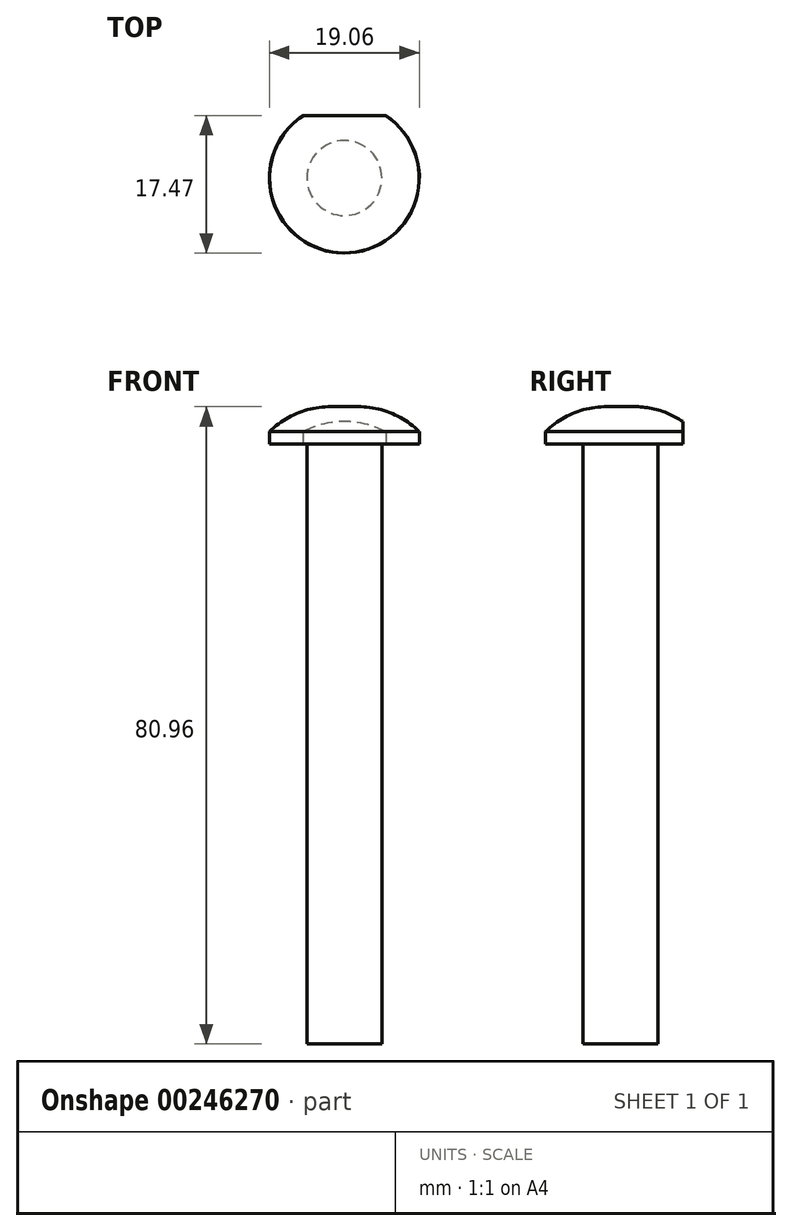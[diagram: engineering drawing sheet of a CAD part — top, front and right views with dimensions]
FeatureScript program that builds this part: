
annotation { "Feature Type Name" : "Feature", "Feature Type Description" : "" }
export const myFeature = defineFeature(function(context is Context, id is Id, definition is map)
    precondition{}
    {
        {
            var Q0;
            Q0=qCreatedBy(makeId("Front.planeOp"),FACE);
            var sketch = newSketch(context, id + "F0", { "sketchPlane" : qUnion([Q0])});
            skLineSegment(sketch, "E0", {"start": v(0, 0) * mm, "end": v(0, 76.2) * mm});
            skLineSegment(sketch, "E1", {"start": v(0, 76.2) * mm, "end": v(0, 77.79) * mm});
            skLineSegment(sketch, "E2", {"start": v(0, 77.79) * mm, "end": v(0, 80.96) * mm});
            skLineSegment(sketch, "E3", {"start": v(0, 80.96) * mm, "end": v(1.72, 80.96) * mm});
            skLineSegment(sketch, "E4", {"start": v(0, 77.79) * mm, "end": v(9.53, 77.79) * mm});
            skPoint(sketch, "E5.visualSharp", {"position": v(6.65, 80.96) * mm});
            skArc(sketch, "E5.filletArc", {"start": v(9.5, 77.79) * mm, "mid": v(5.92, 80.14) * mm, "end": v(1.72, 80.96) * mm});
            skLineSegment(sketch, "E6", {"start": v(0, 76.2) * mm, "end": v(9.53, 76.2) * mm});
            skLineSegment(sketch, "E7", {"start": v(9.53, 76.2) * mm, "end": v(9.53, 77.79) * mm});
            skLineSegment(sketch, "E8", {"start": v(0, 0) * mm, "end": v(4.76, 0) * mm});
            skLineSegment(sketch, "E9", {"start": v(4.76, 0) * mm, "end": v(4.76, 76.2) * mm});
            skSolve(sketch);
        }
        {
            var Q0;
            {var subQ0=sQuery(id+"F0.wireOp",EDGE,"E2");Q0=makeQuery(id+"F0.imprint","IMPRINT",FACE,{"disambiguationData":[TD([[makeQuery(id+"F0.imprint","IMPRINT",EDGE,{"derivedFrom":subQ0}),-1.0]])]});}
            var Q1;
            {var subQ1=sQuery(id+"F0.wireOp",EDGE,"E1");Q1=makeQuery(id+"F0.imprint","IMPRINT",FACE,{"disambiguationData":[TD([[makeQuery(id+"F0.imprint","IMPRINT",EDGE,{"derivedFrom":subQ1}),-1.0]])]});}
            var Q2;
            {var subQ0=sQuery(id+"F0.wireOp",EDGE,"E0");Q2=makeQuery(id+"F0.imprint","IMPRINT",FACE,{"disambiguationData":[TD([[makeQuery(id+"F0.imprint","IMPRINT",EDGE,{"derivedFrom":subQ0}),-1.0]])]});}
            var Q3;
            Q3=sQuery(id+"F0.wireOp",EDGE,"E0");
            revolve(context, id + "F1", {"entities" : qUnion([Q0, Q1, Q2]), "axis" : qUnion([Q3]), "revolveType" : RevolveType.FULL});
        }
        {
            var Q0;
            Q0=makeQuery(id+"F1.opRevolve","SWEPT_FACE",FACE,{"disambiguationData":[OSD([sQuery(id+"F0.wireOp",EDGE,"E3")])]});
            var sketch = newSketch(context, id + "F2", { "sketchPlane" : qUnion([Q0])});
            skCircle(sketch, "E10", {"center": v(0, 0) * mm, "radius": 6.66 * mm});
            skLineSegment(sketch, "E11", {"start": v(0, 0) * mm, "end": v(0, 7.94) * mm});
            skLineSegment(sketch, "E12", {"start": v(0, 7.94) * mm, "end": v(8.71, 7.94) * mm});
            skLineSegment(sketch, "E13", {"start": v(0, 7.94) * mm, "end": v(-8.71, 7.94) * mm});
            skLineSegment(sketch, "E14", {"start": v(8.71, 7.94) * mm, "end": v(8.71, 10.1) * mm});
            skLineSegment(sketch, "E15", {"start": v(8.71, 10.1) * mm, "end": v(-8.71, 10.1) * mm});
            skLineSegment(sketch, "E16", {"start": v(-8.71, 10.1) * mm, "end": v(-8.71, 7.94) * mm});
            skSolve(sketch);
        }
        {
            var Q0;
            Q0=makeQuery(id+"F2.imprint","IMPRINT",FACE,{"disambiguationData":[TD([[makeQuery(id+"F2.imprint","IMPRINT",EDGE,{"derivedFrom":sQuery(id+"F2.wireOp",EDGE,"E12")}),1.0]])]});
            extrude(context, id + "F3", {"entities" : qUnion([Q0]), "operationType" : NewBodyOperationType.REMOVE, "oppositeDirection" : true, "depth" : 25.4 * mm});
        }
    });
